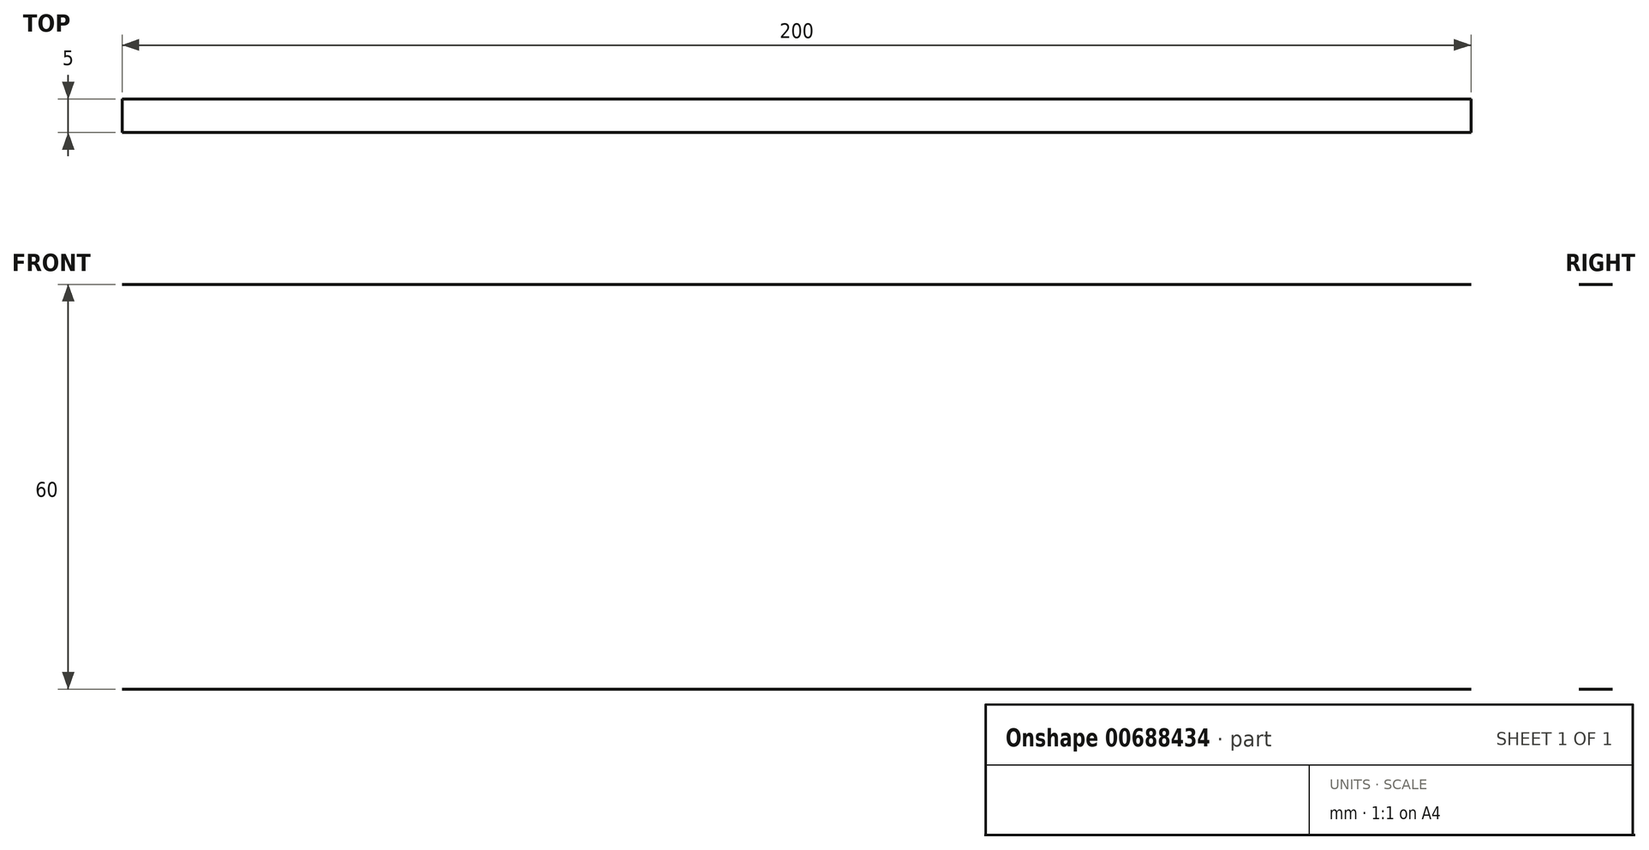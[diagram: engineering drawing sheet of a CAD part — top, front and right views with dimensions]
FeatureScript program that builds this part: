
annotation { "Feature Type Name" : "Feature", "Feature Type Description" : "" }
export const myFeature = defineFeature(function(context is Context, id is Id, definition is map)
    precondition{}
    {
        {
            var Q0;
            Q0=qCreatedBy(makeId("Front.planeOp"),FACE);
            var sketch = newSketch(context, id + "F0", { "sketchPlane" : qUnion([Q0])});
            skLineSegment(sketch, "E0", {"start": v(-59.75, 0) * mm, "end": v(140.25, 0) * mm});
            skLineSegment(sketch, "E1", {"start": v(140.25, 0) * mm, "end": v(140.25, -60) * mm});
            skLineSegment(sketch, "E2", {"start": v(140.25, -60) * mm, "end": v(-59.75, -60) * mm});
            skLineSegment(sketch, "E3", {"start": v(-59.75, -60) * mm, "end": v(-59.75, 0) * mm});
            skLineSegment(sketch, "E4", {"start": v(63.41, -99.4) * mm, "end": v(63.41, -94.91) * mm});
            skSolve(sketch);
        }
        {
            var Q0;
            Q0=sQuery(id+"F0.wireOp",EDGE,"E0");
            var Q1;
            Q1=sQuery(id+"F0.wireOp",EDGE,"E2");
            extrude(context, id + "F1", {"bodyType" : ToolBodyType.SURFACE, "surfaceEntities" : qUnion([Q0, Q1]), "depth" : 5 * mm, "offsetDistance" : 25 * mm});
        }
    });
